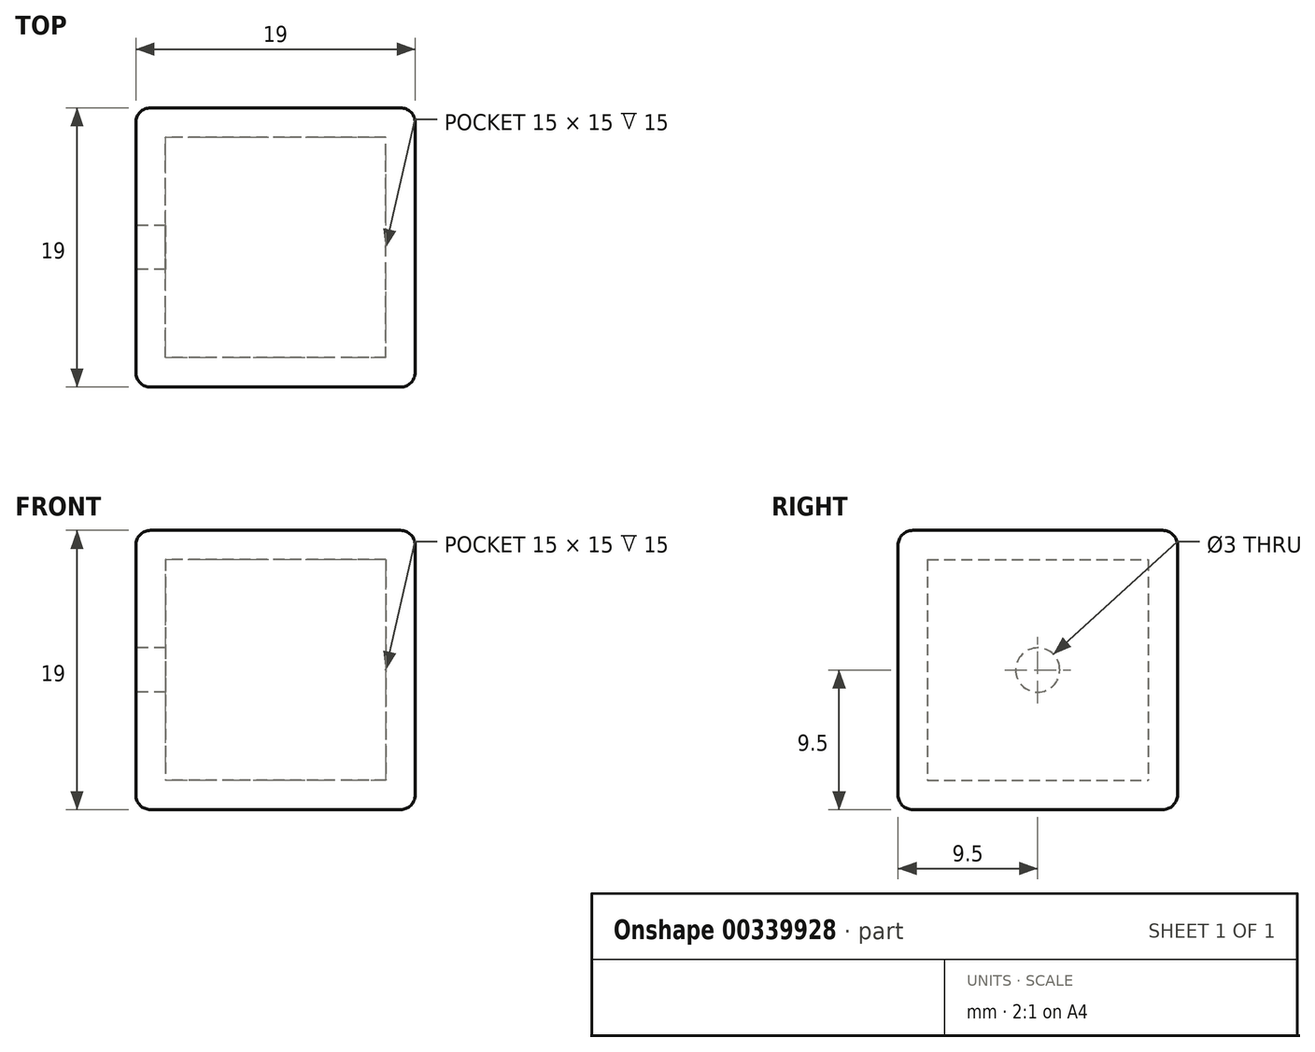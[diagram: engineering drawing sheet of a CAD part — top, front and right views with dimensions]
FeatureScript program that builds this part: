
annotation { "Feature Type Name" : "Feature", "Feature Type Description" : "" }
export const myFeature = defineFeature(function(context is Context, id is Id, definition is map)
    precondition{}
    {
        {
            var Q0;
            Q0=qCreatedBy(makeId("Top.planeOp"),FACE);
            var sketch = newSketch(context, id + "F0", { "sketchPlane" : qUnion([Q0])});
            skLineSegment(sketch, "E0.bottom", {"start": v(-9.5, -9.5) * mm, "end": v(9.5, -9.5) * mm});
            skLineSegment(sketch, "E0.top", {"start": v(-9.5, 9.5) * mm, "end": v(9.5, 9.5) * mm});
            skLineSegment(sketch, "E0.left", {"start": v(-9.5, -9.5) * mm, "end": v(-9.5, 9.5) * mm});
            skLineSegment(sketch, "E0.right", {"start": v(9.5, -9.5) * mm, "end": v(9.5, 9.5) * mm});
            skPoint(sketch, "E0.middle", {"position": v(0, 0) * mm});
            skSolve(sketch);
        }
        {
            var Q0;
            Q0=makeQuery(id+"F0.imprint","IMPRINT",FACE,{"disambiguationData":[TD([[makeQuery(id+"F0.imprint","IMPRINT",EDGE,{"derivedFrom":sQuery(id+"F0.wireOp",EDGE,"E0.bottom")}),1.0]])]});
            extrude(context, id + "F1", {"entities" : qUnion([Q0]), "endBound" : BoundingType.SYMMETRIC, "depth" : 19 * mm});
        }
        {
            var Q0;
            Q0=makeQuery(id+"F1.opExtrude","SWEPT_FACE",FACE,{"disambiguationData":[OSD([sQuery(id+"F0.wireOp",EDGE,"E0.left")])]});
            var sketch = newSketch(context, id + "F2", { "sketchPlane" : qUnion([Q0])});
            skLineSegment(sketch, "E1", {"start": v(-9.5, 9.5) * mm, "end": v(9.5, -10) * mm, "construction": true});
            skLineSegment(sketch, "E2.bottom", {"start": v(7.5, 7.5) * mm, "end": v(-7.5, 7.5) * mm});
            skLineSegment(sketch, "E2.top", {"start": v(7.5, -7.5) * mm, "end": v(-7.5, -7.5) * mm});
            skLineSegment(sketch, "E2.left", {"start": v(7.5, 7.5) * mm, "end": v(7.5, -7.5) * mm});
            skLineSegment(sketch, "E2.right", {"start": v(-7.5, 7.5) * mm, "end": v(-7.5, -7.5) * mm});
            skPoint(sketch, "E2.middle", {"position": v(0, 0) * mm});
            skSolve(sketch);
        }
        {
            var Q0;
            Q0=makeQuery(id+"F2.imprint","IMPRINT",FACE,{"disambiguationData":[TD([[makeQuery(id+"F2.imprint","IMPRINT",EDGE,{"derivedFrom":sQuery(id+"F2.wireOp",EDGE,"E2.bottom")}),1.0]])]});
            extrude(context, id + "F3", {"entities" : qUnion([Q0]), "operationType" : NewBodyOperationType.REMOVE, "oppositeDirection" : true, "depth" : 17 * mm, "hasSecondDirection" : true, "secondDirectionOppositeDirection" : false, "secondDirectionDepth" : -2 * mm});
        }
        {
            var Q0;
            Q0=makeQuery(id+"F1.opExtrude","SWEPT_FACE",FACE,{"disambiguationData":[OSD([sQuery(id+"F0.wireOp",EDGE,"E0.left")])]});
            var sketch = newSketch(context, id + "F4", { "sketchPlane" : qUnion([Q0])});
            skCircle(sketch, "E3", {"center": v(0, 0) * mm, "radius": 1.5 * mm});
            skSolve(sketch);
        }
        {
            var Q0;
            Q0=makeQuery(id+"F1.opExtrude","CAP_EDGE",EDGE,{"disambiguationData":[OSD([sQuery(id+"F0.wireOp",EDGE,"E0.left")])],"isStart":false});
            var Q1;
            Q1=makeQuery(id+"F1.opExtrude","CAP_EDGE",EDGE,{"disambiguationData":[OSD([sQuery(id+"F0.wireOp",EDGE,"E0.bottom")])],"isStart":false});
            var Q2;
            Q2=makeQuery(id+"F1.opExtrude","CAP_FACE",FACE,{"disambiguationData":[OSD([sQuery(id+"F0.wireOp",EDGE,"E0.bottom"),sQuery(id+"F0.wireOp",EDGE,"E0.top"),sQuery(id+"F0.wireOp",EDGE,"E0.left"),sQuery(id+"F0.wireOp",EDGE,"E0.right")])],"isStart":false});
            var Q3;
            Q3=makeQuery(id+"F1.opExtrude","SWEPT_EDGE",EDGE,{"disambiguationData":[OSD([sQuery(id+"F0.wireOp",EDGE,"E0.top"),sQuery(id+"F0.wireOp",EDGE,"E0.left")])]});
            var Q4;
            Q4=makeQuery(id+"F1.opExtrude","SWEPT_EDGE",EDGE,{"disambiguationData":[OSD([sQuery(id+"F0.wireOp",EDGE,"E0.top"),sQuery(id+"F0.wireOp",EDGE,"E0.right")])]});
            var Q5;
            Q5=makeQuery(id+"F1.opExtrude","CAP_EDGE",EDGE,{"disambiguationData":[OSD([sQuery(id+"F0.wireOp",EDGE,"E0.top")])],"isStart":true});
            var Q6;
            Q6=makeQuery(id+"F1.opExtrude","SWEPT_EDGE",EDGE,{"disambiguationData":[OSD([sQuery(id+"F0.wireOp",EDGE,"E0.bottom"),sQuery(id+"F0.wireOp",EDGE,"E0.right")])]});
            var Q7;
            Q7=makeQuery(id+"F1.opExtrude","CAP_EDGE",EDGE,{"disambiguationData":[OSD([sQuery(id+"F0.wireOp",EDGE,"E0.bottom")])],"isStart":true});
            var Q8;
            Q8=makeQuery(id+"F1.opExtrude","CAP_EDGE",EDGE,{"disambiguationData":[OSD([sQuery(id+"F0.wireOp",EDGE,"E0.right")])],"isStart":true});
            var Q9;
            Q9=makeQuery(id+"F1.opExtrude","SWEPT_EDGE",EDGE,{"disambiguationData":[OSD([sQuery(id+"F0.wireOp",EDGE,"E0.bottom"),sQuery(id+"F0.wireOp",EDGE,"E0.left")])]});
            var Q10;
            Q10=makeQuery(id+"F1.opExtrude","CAP_EDGE",EDGE,{"disambiguationData":[OSD([sQuery(id+"F0.wireOp",EDGE,"E0.left")])],"isStart":true});
            fillet(context, id + "F5", {"entities" : qUnion([Q0, Q1, Q2, Q3, Q4, Q5, Q6, Q7, Q8, Q9, Q10]), "radius" : 1 * mm, "tangentPropagation" : true, "allowEdgeOverflow" : false});
        }
        {
            var Q0;
            Q0=makeQuery(id+"F4.imprint","IMPRINT",FACE,{"disambiguationData":[TD([[makeQuery(id+"F4.imprint","IMPRINT",EDGE,{"derivedFrom":sQuery(id+"F4.wireOp",EDGE,"E3")}),1.0]])]});
            extrude(context, id + "F6", {"entities" : qUnion([Q0]), "operationType" : NewBodyOperationType.REMOVE, "oppositeDirection" : true, "depth" : 2 * mm});
        }
    });
